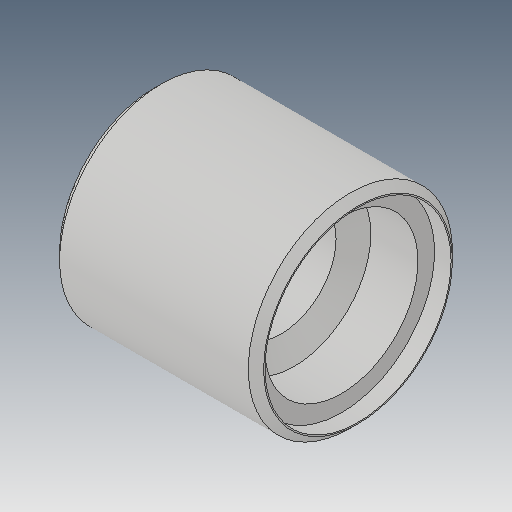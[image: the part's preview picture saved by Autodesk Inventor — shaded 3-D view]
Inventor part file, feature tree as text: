
AUTODESK INVENTOR PART (.ipt)
format: ipt  version: 2019.4 (Build 234330000, 330)  size: 147,456 bytes
history: native  units: mm
features: sketch x2, other x1, revolve x1, chamfer x1, hole x1, mirror x1
ambient origin geometry x8: Origin, YZ Plane, XZ Plane, XY Plane, X Axis, Y Axis, Z Axis, Center Point
bodies: Body1 (feature_tree)
feature tree (7):
  other  "ソリッド1"
  revolve  "回転1"
  chamfer  "面取り1"  Distance=8.0mm
  hole  "穴1"  [1 undecoded]
  mirror  "ミラー1"
  sketch  "スケッチ1"
  sketch  "スケッチ2"
note: 1 required parameter value undecoded (feature->parameter linkage not recoverable at this tier; creation-order binding heuristic only, values carry confidence <= 0.55)
